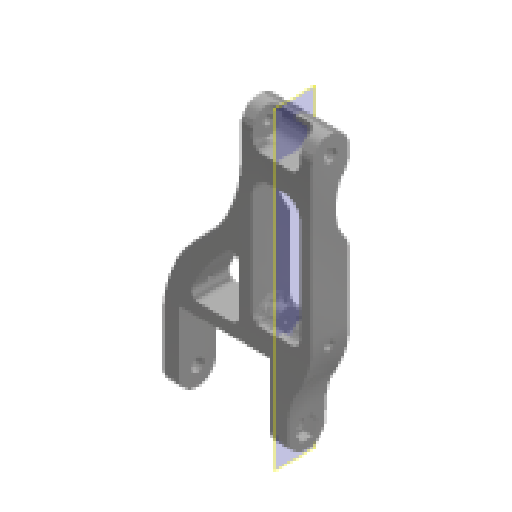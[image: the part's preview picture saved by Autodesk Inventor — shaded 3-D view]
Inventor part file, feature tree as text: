
AUTODESK INVENTOR PART (.ipt)
format: ipt  version: 2025 (Build 290162000, 162)  size: 531,456 bytes
history: native  units: in
note: dims shown in document units (in); Inventor stores cm internally (conversion verified against a paired STEP export)
features: extrude x15, sketch x15, projected_geometry x13, fillet x11, plane x5, mirror x3, other x3, reference x1
ambient origin geometry x8: Origin, YZ Plane, XZ Plane, XY Plane, X Axis, Y Axis, Z Axis, Center Point
bodies: Solid1 (feature_tree)
feature tree (66):
  extrude  "Extrusion1"  Depth=0.315in TaperAngle=0.0deg
  extrude  "Extrusion2"  Depth=0.2559in
  extrude  "Extrusion3"  Depth=0.1181in
  plane  "Work Plane1"
  mirror  "Mirror1"
  extrude  "Extrusion4"  Depth=0.315in TaperAngle=0.0deg
  extrude  "Extrusion5"  Depth=0.5in
  fillet  "Fillet1"  Radius=1.0in
  extrude  "Extrusion6"  Depth=0.25in
  fillet  "Fillet2"  [1 undecoded]
  fillet  "Fillet4"  Radius=0.3228in
  plane  "Work Plane2"
  extrude  "Extrusion7"  Depth=1.5in
  fillet  "Fillet5"  Radius=0.2362in
  extrude  "Extrusion8"  Depth=0.3937in
  fillet  "Fillet6"  Radius=0.3937in
  extrude  "Extrusion9"  Depth=0.3937in TaperAngle=0.0deg
  mirror  "Mirror2"
  fillet  "Fillet7"  Radius=1.5507in
  sketch  "Sketch10"  dims[d38=0.4724in d39=0.0in d40=3.0in]
  plane  "Work Plane3"
  extrude  "Extrusion10"  Depth=3.0in
  sketch  "Sketch11"  dims[d41=0.2362in d42=0.0in d43=0.0in d44=0.0in]
  plane  "Work Plane4"
  extrude  "Extrusion11"  TaperAngle=0.0deg  [1 undecoded]
  extrude  "Extrusion12"  Depth=0.5087in
  fillet  "Fillet8"  Radius=0.1969in
  extrude  "Extrusion13"  Depth=0.25in
  extrude  "Extrusion14"  TaperAngle=0.0deg  [1 undecoded]
  fillet  "Fillet9"  [1 undecoded]
  fillet  "Fillet10"  [1 undecoded]
  fillet  "Fillet12"  [1 undecoded]
  fillet  "Fillet13"  [1 undecoded]
  extrude  "Extrusion15"  [1 undecoded]
  mirror  "Mirror3"
  plane  "Work Plane5"
  sketch  "Sketch1"  dims[d0=0.3346in d1=0.315in d2=0.0in]
  sketch  "Sketch2"  dims[d3=0.0787in d4=0.0in d5=0.2559in]
  projected_geometry  "Projected Loop1"
  sketch  "Sketch3"  dims[d6=0.1181in d7=0.0in d8=0.1181in]
  projected_geometry  "Projected Loop2"
  sketch  "Sketch4"  dims[d9=0.6102in d10=0.315in d11=0.0in]
  projected_geometry  "Projected Loop3"
  sketch  "Sketch5"  dims[d12=0.0in d13=0.0in d14=0.5in d15=1.0in d16=0.0in]
  projected_geometry  "Projected Loop4"
  sketch  "Sketch6"  dims[d17=0.25in d19=0.4in d20=-1.0836in d21=0.3228in]
  projected_geometry  "Projected Loop5"
  sketch  "Sketch7"  dims[d22=0.4724in d23=0.0in d24=1.5in d25=0.2362in]
  projected_geometry  "Projected Loop6"
  reference  "Reference1"
  sketch  "Sketch8"  dims[d26=0.1575in d27=0.0in d28=2.0in d29=0.3937in d30=0.0in]
  sketch  "Sketch9"  dims[d31=0.25in d33=-0.2362in d34=0.3937in d35=0.0in d36=1.5507in d37=0.0in]
  projected_geometry  "Projected Loop7"
  projected_geometry  "Projected Loop8"
  projected_geometry  "Projected Loop9"
  sketch  "Sketch12"  dims[d45=0.1969in d46=0.5087in d47=0.1969in]
  projected_geometry  "Projected Loop10"
  projected_geometry  "Projected Loop11"
  sketch  "Sketch13"  dims[d49=0.25in d50=0.25in]
  sketch  "Sketch14"  dims[d51=0.0591in d52=0.0in d48=0.0in]
  projected_geometry  "Projected Loop12"
  sketch  "Sketch15"
  projected_geometry  "Projected Loop13"
  other  "<userpath>\Desktop\puppycat\singleSwingarmV2.iam"
  other  "singleSwingarmV2.iam"
  other  "6082rsBearing:3"
note: 8 required parameter values undecoded (feature->parameter linkage not recoverable at this tier; creation-order binding heuristic only, values carry confidence <= 0.55)
